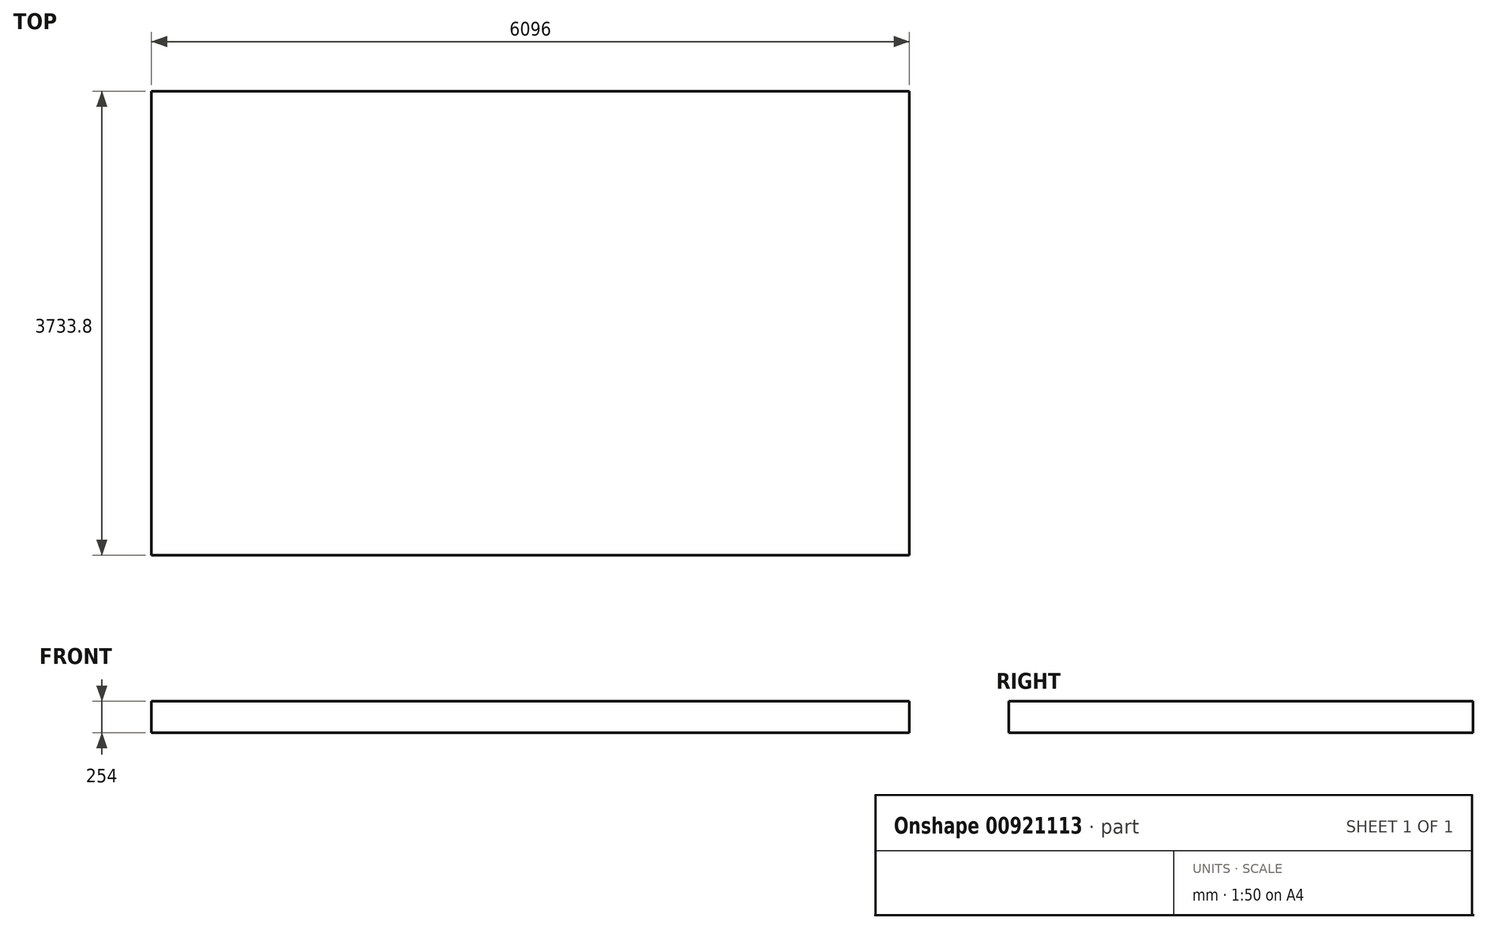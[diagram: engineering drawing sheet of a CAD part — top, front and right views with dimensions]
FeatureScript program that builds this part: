
annotation { "Feature Type Name" : "Feature", "Feature Type Description" : "" }
export const myFeature = defineFeature(function(context is Context, id is Id, definition is map)
    precondition{}
    {
        {
            var Q0;
            Q0=qCreatedBy(makeId("Top.planeOp"),FACE);
            var sketch = newSketch(context, id + "F0", { "sketchPlane" : qUnion([Q0])});
            skLineSegment(sketch, "E0.bottom", {"start": v(0, 0) * mm, "end": v(-6096, 0) * mm});
            skLineSegment(sketch, "E0.top", {"start": v(0, 3733.8) * mm, "end": v(-6096, 3733.8) * mm});
            skLineSegment(sketch, "E0.left", {"start": v(0, 0) * mm, "end": v(0, 3733.8) * mm});
            skLineSegment(sketch, "E0.right", {"start": v(-6096, 0) * mm, "end": v(-6096, 3733.8) * mm});
            skSolve(sketch);
        }
        {
            var Q0;
            Q0=makeQuery(id+"F0.imprint","IMPRINT",FACE,{"disambiguationData":[TD([[makeQuery(id+"F0.imprint","IMPRINT",EDGE,{"derivedFrom":sQuery(id+"F0.wireOp",EDGE,"E0.bottom")}),-1.0]])]});
            extrude(context, id + "F1", {"entities" : qUnion([Q0]), "oppositeDirection" : true, "depth" : 254 * mm, "offsetDistance" : 25.4 * mm});
        }
        {
            var Q0;
            Q0=makeQuery(id+"F1.opExtrude","SWEPT_BODY",BODY,{"disambiguationData":[OSD([sQuery(id+"F0.wireOp",EDGE,"E0.bottom"),sQuery(id+"F0.wireOp",EDGE,"E0.top"),sQuery(id+"F0.wireOp",EDGE,"E0.left"),sQuery(id+"F0.wireOp",EDGE,"E0.right")])]});
            var Q1;
            Q1=makeQuery(id+"F1.opExtrude","SWEPT_BODY",BODY,{"disambiguationData":[OSD([sQuery(id+"F0.wireOp",EDGE,"E0.bottom"),sQuery(id+"F0.wireOp",EDGE,"E0.top"),sQuery(id+"F0.wireOp",EDGE,"E0.left"),sQuery(id+"F0.wireOp",EDGE,"E0.right")])]});
            transform(context, id + "F2", {"entities" : qUnion([Q0, Q1]), "transformType" : TransformType.TRANSLATION_3D, "dx" : 0 * mm, "dy" : 0 * mm, "dz" : 0 * mm, "makeCopy" : true});
        }
        {
            var Q0;
            Q0=makeQuery(id+"F2.opPattern","COPY",BODY,{"derivedFrom":makeQuery(id+"F1.opExtrude","SWEPT_BODY",BODY,{"disambiguationData":[OSD([sQuery(id+"F0.wireOp",EDGE,"E0.bottom"),sQuery(id+"F0.wireOp",EDGE,"E0.top"),sQuery(id+"F0.wireOp",EDGE,"E0.left"),sQuery(id+"F0.wireOp",EDGE,"E0.right")])]}),"instanceName":"1"});
            deleteBodies(context, id + "F3", {"entities" : qUnion([Q0])});
        }
        {
            var Q0;
            Q0=makeQuery(id+"F1.opExtrude","SWEPT_FACE",FACE,{"disambiguationData":[OSD([sQuery(id+"F0.wireOp",EDGE,"E0.right")])]});
            var sketch = newSketch(context, id + "F4", { "sketchPlane" : qUnion([Q0])});
            skLineSegment(sketch, "E1", {"start": v(-3733.8, -127) * mm, "end": v(-3581.4, -127) * mm, "construction": true});
            skPoint(sketch, "E2", {"position": v(-3581.4, -127) * mm});
            skSolve(sketch);
        }
        {
            var Q0;
            Q0=makeQuery(id+"F1.opExtrude","SWEPT_FACE",FACE,{"disambiguationData":[OSD([sQuery(id+"F0.wireOp",EDGE,"E0.left")])]});
            var sketch = newSketch(context, id + "F5", { "sketchPlane" : qUnion([Q0])});
            skLineSegment(sketch, "E3", {"start": v(3733.8, -127) * mm, "end": v(3581.4, -127) * mm, "construction": true});
            skSolve(sketch);
        }
    });
